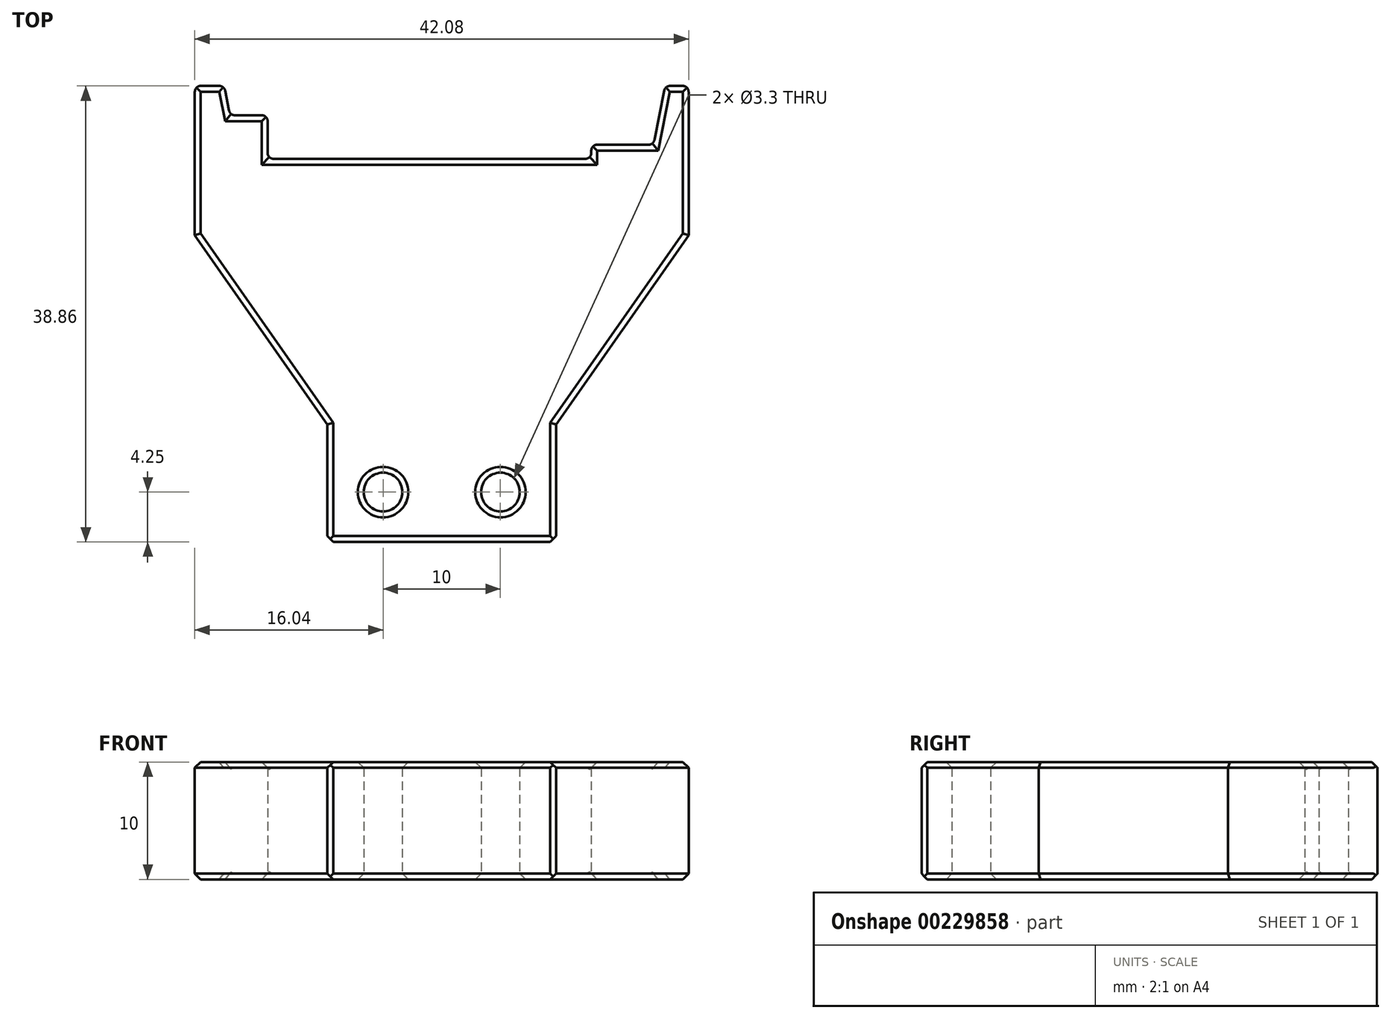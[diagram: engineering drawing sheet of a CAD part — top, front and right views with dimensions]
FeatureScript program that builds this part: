
annotation { "Feature Type Name" : "Feature", "Feature Type Description" : "" }
export const myFeature = defineFeature(function(context is Context, id is Id, definition is map)
    precondition{}
    {
        {
            var Q0;
            Q0=qCreatedBy(makeId("Top.planeOp"),FACE);
            var sketch = newSketch(context, id + "F0", { "sketchPlane" : qUnion([Q0])});
            skLineSegment(sketch, "E0.left", {"start": v(21.03, 6.69) * mm, "end": v(21.03, 19.43) * mm});
            skPoint(sketch, "E0.middle", {"position": v(0, 0) * mm});
            skLineSegment(sketch, "E1.left", {"start": v(9.75, -19.43) * mm, "end": v(9.75, -9.43) * mm});
            skLineSegment(sketch, "E2", {"start": v(9.75, -9.43) * mm, "end": v(21.04, 6.69) * mm});
            skPoint(sketch, "E3.orphan", {"position": v(21.04, -19.38) * mm});
            skLineSegment(sketch, "E4.MirrorCS", {"start": v(-9.75, -19.43) * mm, "end": v(-9.75, -9.43) * mm});
            skLineSegment(sketch, "E5.MirrorCS", {"start": v(-21.04, 6.69) * mm, "end": v(-21.04, 19.43) * mm});
            skLineSegment(sketch, "E6.MirrorCS", {"start": v(-9.75, -9.43) * mm, "end": v(-21.04, 6.69) * mm});
            skLineSegment(sketch, "E7", {"start": v(-9.75, -19.43) * mm, "end": v(9.75, -19.43) * mm});
            skLineSegment(sketch, "E8", {"start": v(-21.04, 19.43) * mm, "end": v(-18.53, 19.43) * mm});
            skLineSegment(sketch, "E9", {"start": v(-18.53, 19.43) * mm, "end": v(-18.04, 16.93) * mm});
            skLineSegment(sketch, "E10", {"start": v(-18.04, 16.93) * mm, "end": v(-14.84, 16.93) * mm});
            skLineSegment(sketch, "E11", {"start": v(-14.84, 16.93) * mm, "end": v(-14.84, 13.22) * mm});
            skLineSegment(sketch, "E12", {"start": v(-14.84, 13.22) * mm, "end": v(12.75, 13.22) * mm});
            skLineSegment(sketch, "E13", {"start": v(12.75, 13.22) * mm, "end": v(12.75, 14.42) * mm});
            skLineSegment(sketch, "E14", {"start": v(12.75, 14.42) * mm, "end": v(18.04, 14.42) * mm});
            skLineSegment(sketch, "E15", {"start": v(18.03, 14.42) * mm, "end": v(19.04, 19.43) * mm});
            skLineSegment(sketch, "E16", {"start": v(19.04, 19.43) * mm, "end": v(21.04, 19.43) * mm});
            skPoint(sketch, "E17", {"position": v(-5, -15.18) * mm});
            skPoint(sketch, "E18", {"position": v(5, -15.18) * mm});
            skSolve(sketch);
        }
        {
            var Q0;
            Q0=makeQuery(id+"F0.imprint","IMPRINT",FACE,{"disambiguationData":[TD([[makeQuery(id+"F0.imprint","IMPRINT",EDGE,{"derivedFrom":sQuery(id+"F0.wireOp",EDGE,"E0.left")}),1.0]])]});
            extrude(context, id + "F1", {"entities" : qUnion([Q0]), "depth" : 10 * mm});
        }
        {
            var Q0;
            Q0=sQuery(id+"F0.wireOp",VERTEX,"E18");
            var Q1;
            Q1=sQuery(id+"F0.wireOp",VERTEX,"E17");
            var Q2;
            Q2=makeQuery(id+"F1.opExtrude","SWEPT_BODY",BODY,{"disambiguationData":[OSD([sQuery(id+"F0.wireOp",EDGE,"E0.left"),sQuery(id+"F0.wireOp",EDGE,"E1.left"),sQuery(id+"F0.wireOp",EDGE,"E2"),sQuery(id+"F0.wireOp",EDGE,"E4.MirrorCS"),sQuery(id+"F0.wireOp",EDGE,"E5.MirrorCS"),sQuery(id+"F0.wireOp",EDGE,"E6.MirrorCS"),sQuery(id+"F0.wireOp",EDGE,"E7"),sQuery(id+"F0.wireOp",EDGE,"E8"),sQuery(id+"F0.wireOp",EDGE,"E9"),sQuery(id+"F0.wireOp",EDGE,"E10"),sQuery(id+"F0.wireOp",EDGE,"E11"),sQuery(id+"F0.wireOp",EDGE,"E12"),sQuery(id+"F0.wireOp",EDGE,"E13"),sQuery(id+"F0.wireOp",EDGE,"E14"),sQuery(id+"F0.wireOp",EDGE,"E15"),sQuery(id+"F0.wireOp",EDGE,"E16")])]});
            hole(context, id + "F2", {"style" : HoleStyle.SIMPLE, "endStyle" : HoleEndStyle.THROUGH, "oppositeDirection" : true, "standardTappedOrClearance" : lookupTablePath({ "standard" : "ISO", "fit" : "Normal", "size" : "M3", "type" : "Clearance" }), "standardBlindInLast" : lookupTablePath({ "fit" : "Standard", "standard" : "ISO", "size" : "M3", "type" : "Clearance" }), "holeDiameter" : 3.3 * mm, "startFromSketch" : true, "locations" : qUnion([Q0, Q1]), "scope" : qUnion([Q2]), "isTappedThrough" : true});
        }
        {
            var Q0;
            Q0=makeQuery(id+"F1.opExtrude","CAP_FACE",FACE,{"disambiguationData":[OSD([sQuery(id+"F0.wireOp",EDGE,"E0.left"),sQuery(id+"F0.wireOp",EDGE,"E1.left"),sQuery(id+"F0.wireOp",EDGE,"E2"),sQuery(id+"F0.wireOp",EDGE,"E4.MirrorCS"),sQuery(id+"F0.wireOp",EDGE,"E5.MirrorCS"),sQuery(id+"F0.wireOp",EDGE,"E6.MirrorCS"),sQuery(id+"F0.wireOp",EDGE,"E7"),sQuery(id+"F0.wireOp",EDGE,"E8"),sQuery(id+"F0.wireOp",EDGE,"E9"),sQuery(id+"F0.wireOp",EDGE,"E10"),sQuery(id+"F0.wireOp",EDGE,"E11"),sQuery(id+"F0.wireOp",EDGE,"E12"),sQuery(id+"F0.wireOp",EDGE,"E13"),sQuery(id+"F0.wireOp",EDGE,"E14"),sQuery(id+"F0.wireOp",EDGE,"E15"),sQuery(id+"F0.wireOp",EDGE,"E16")])],"isStart":false});
            var Q1;
            Q1=makeQuery(id+"F1.opExtrude","CAP_FACE",FACE,{"disambiguationData":[OSD([sQuery(id+"F0.wireOp",EDGE,"E0.left"),sQuery(id+"F0.wireOp",EDGE,"E1.left"),sQuery(id+"F0.wireOp",EDGE,"E2"),sQuery(id+"F0.wireOp",EDGE,"E4.MirrorCS"),sQuery(id+"F0.wireOp",EDGE,"E5.MirrorCS"),sQuery(id+"F0.wireOp",EDGE,"E6.MirrorCS"),sQuery(id+"F0.wireOp",EDGE,"E7"),sQuery(id+"F0.wireOp",EDGE,"E8"),sQuery(id+"F0.wireOp",EDGE,"E9"),sQuery(id+"F0.wireOp",EDGE,"E10"),sQuery(id+"F0.wireOp",EDGE,"E11"),sQuery(id+"F0.wireOp",EDGE,"E12"),sQuery(id+"F0.wireOp",EDGE,"E13"),sQuery(id+"F0.wireOp",EDGE,"E14"),sQuery(id+"F0.wireOp",EDGE,"E15"),sQuery(id+"F0.wireOp",EDGE,"E16")])],"isStart":true});
            chamfer(context, id + "F3", {"entities" : qUnion([Q0, Q1]), "width" : .5 * mm, "tangentPropagation" : true});
        }
        {
            var Q0;
            Q0=makeQuery(id+"F1.opExtrude","SWEPT_EDGE",EDGE,{"disambiguationData":[OSD([sQuery(id+"F0.wireOp",EDGE,"E5.MirrorCS"),sQuery(id+"F0.wireOp",EDGE,"E8")])]});
            var Q1;
            Q1=makeQuery(id+"F1.opExtrude","SWEPT_EDGE",EDGE,{"disambiguationData":[OSD([sQuery(id+"F0.wireOp",EDGE,"E8"),sQuery(id+"F0.wireOp",EDGE,"E9")])]});
            var Q2;
            Q2=makeQuery(id+"F1.opExtrude","SWEPT_EDGE",EDGE,{"disambiguationData":[OSD([sQuery(id+"F0.wireOp",EDGE,"E9"),sQuery(id+"F0.wireOp",EDGE,"E10")])]});
            var Q3;
            Q3=makeQuery(id+"F1.opExtrude","SWEPT_EDGE",EDGE,{"disambiguationData":[OSD([sQuery(id+"F0.wireOp",EDGE,"E10"),sQuery(id+"F0.wireOp",EDGE,"E11")])]});
            var Q4;
            Q4=makeQuery(id+"F1.opExtrude","SWEPT_EDGE",EDGE,{"disambiguationData":[OSD([sQuery(id+"F0.wireOp",EDGE,"E11"),sQuery(id+"F0.wireOp",EDGE,"E12")])]});
            var Q5;
            Q5=makeQuery(id+"F1.opExtrude","SWEPT_EDGE",EDGE,{"disambiguationData":[OSD([sQuery(id+"F0.wireOp",EDGE,"E0.left"),sQuery(id+"F0.wireOp",EDGE,"E16")])]});
            var Q6;
            Q6=makeQuery(id+"F1.opExtrude","SWEPT_EDGE",EDGE,{"disambiguationData":[OSD([sQuery(id+"F0.wireOp",EDGE,"E15"),sQuery(id+"F0.wireOp",EDGE,"E16")])]});
            var Q7;
            Q7=makeQuery(id+"F1.opExtrude","SWEPT_EDGE",EDGE,{"disambiguationData":[OSD([sQuery(id+"F0.wireOp",EDGE,"E14"),sQuery(id+"F0.wireOp",EDGE,"E15")])]});
            var Q8;
            Q8=makeQuery(id+"F1.opExtrude","SWEPT_EDGE",EDGE,{"disambiguationData":[OSD([sQuery(id+"F0.wireOp",EDGE,"E13"),sQuery(id+"F0.wireOp",EDGE,"E14")])]});
            var Q9;
            Q9=makeQuery(id+"F1.opExtrude","SWEPT_EDGE",EDGE,{"disambiguationData":[OSD([sQuery(id+"F0.wireOp",EDGE,"E12"),sQuery(id+"F0.wireOp",EDGE,"E13")])]});
            fillet(context, id + "F4", {"entities" : qUnion([Q0, Q1, Q2, Q3, Q4, Q5, Q6, Q7, Q8, Q9]), "radius" : .5 * mm, "tangentPropagation" : true, "allowEdgeOverflow" : false});
        }
        {
            var Q0;
            Q0=makeQuery(id+"F1.opExtrude","SWEPT_EDGE",EDGE,{"disambiguationData":[OSD([sQuery(id+"F0.wireOp",EDGE,"E4.MirrorCS"),sQuery(id+"F0.wireOp",EDGE,"E7")])]});
            var Q1;
            Q1=makeQuery(id+"F1.opExtrude","SWEPT_EDGE",EDGE,{"disambiguationData":[OSD([sQuery(id+"F0.wireOp",EDGE,"E1.left"),sQuery(id+"F0.wireOp",EDGE,"E7")])]});
            chamfer(context, id + "F5", {"entities" : qUnion([Q0, Q1]), "width" : .5 * mm, "tangentPropagation" : true});
        }
    });
